# Revit family: IS_ConnectSpace_E1333_BIM_FR
name_source: partatom
category: Plumbing Fixtures
revit_build: Autodesk Revit MEP 2016 (Build: 20161004_0715(x64)
units: mm (PartAtom-declared; Revit-internal decimal feet)

## family parameters
Always vertical = No
Cut with Voids When Loaded = No
OmniClass Number = 23.45.05.14.14
OmniClass Title = Sinks/Lavatories
Part Type = Normal
Room Calculation Point = No
Round Connector Dimension = Use Diameter
Shared = No
Work Plane-Based = No

## types (1)
- E1333 - Lavabo 55 x 38 cm
    Accessoires = www.idealspec.fr
    Assembly Code = C1030200
    Auteur = Ideal Standard (Fr)
    BIMobject category = Basins
    BOSUseNativeGeometries = 1
    Brand url = http://www.idealstandard.co.uk
    Caracteristiques = Lavabo 55 x 38 cm
    CodeBarre = 5017830447672
    ConseilsDInstallation = http://www.idealspec.fr
    Couleur = blanc
    CoutDeRemplacement = 0
    DateDeCreation = 26.07.2018
    DebitL/Mn = Litres
    Description = Lavabo 55 x 38 cm
    DetailGarantie = Manufacturers Warranty
    Dimensions = 172 x 551 x 380
    DureeDeGarantieDesPieces = 2
    DureeGarantie = year
    EAN code = https://5017830447672
    Edition number = 1
    Espace = Internal
    Finition = blanc
    Forme = Sculptured
    Hauteur = 172 mm
    IFC Classification = Sanitary Terminal
    IfcExportAs = IfcSanitaryType
    IfcExportType = WASHHANDBASIN
    InformationsProduit = http://www.idealspec.fr
    Installation instructions = http://www.idealstandard.it
    Largeur = 551 mm
    LienUtile = www.idealspec.fr
    Longueur = 380 mm
    Manufacturer name = Ideal Standard
    Marque = Ideal Standard
    Material main = Ceramics
    Materiel = Vitreous china
    Model = E1333
    NBS Reference Code = 35-79-18
    NBS Reference Description = Counter Top Wash Basins
    Nom = Lavabo 55 x 38 cm
    Nominal height = 175
    Nominal width = 550
    OmniClass Code = 23-31 13 00
    OmniClass Description = Sinks
    PoidsBrut = 13.5
    PoidsNet = 13.5
    Product Guid = 9c8bf3f0-2e0c-4aad-bb05-daa5e6eb00a1
    Product SKU = E1333
    Product certification = http://www.idealstandard.it
    Product data url = https://bimobject.com
    Product family = CONNECT SPACE
    Product group = Basin
    Product name = CONNECT SPACE BASIN 55X38 WHITE SPHERE LP
    Product url = http://www.idealstandard.it
    QR code = http://bimobject.com
    Revision = 1
    Technical description = http://www.idealstandard.it
    TypeDeLavabo = Washbasins
    URL = www.idealspec.fr
    Uniclass 1.4 Code = L7212
    Uniclass 1.4 Description = Washbasins
    Uniclass 2.0 Code = PR-35-79-94
    Uniclass 2.0 Description = Wall-Hung Wash Basins
    Uniclass 2015 Code = Pr_40_20_96_96
    Uniclass 2015 Name = Wall-hung wash basins
    UrlDuFabricant = www.idealspec.fr
    Weight Net (Kg) = 13.5

## geometry (parser evidence)
native form markers: Blend x4, Sweep x1
no freeform markers — native parametric forms only
